# Revit family: Gleitschlitten Typ C, höhe h=200mm, Ø219 bis Ø457mm, m.D
name_source: partatom
category: HLS-Bauteile
revit_build: Autodesk Revit 2018 (Build: 20190510_1515(x64)
units: mm (PartAtom-declared; Revit-internal decimal feet)

## family parameters
Arbeitsebenenbasiert = Ja
Beim Laden mit Abzugskörper schneiden = Nein
Bemaßung runder Anschluss = Durchmesser verwenden
Gemeinsam genutzt = Ja
Immer vertikal = Nein
Klassifizierung = Keine
Raumberechnungspunkt = Nein
Teiletyp = Normal

## types (11) — shared parameters
Baustoffklasse = B2
Breite Schellenband = 50 mm
Dämmstärke = 6 mm  [stored 0.019685 ft]
Fabrikat = MEFA
Kurztext1 = Gleitschlitten C 50 x 5 mm
L = 190 mm  [stored 0.62336 ft]
Mengeneinheit = St
Schalldämmeinlage = Gummi EPDM
Sicherheitsfaktor = 1.54
Stärke Schellenband = 5 mm
Verschluss = Schraube + Mutter
Verschluss-Schraube = M12
Vorgabe-Ansicht = 1219 mm
max. Temperaturbeständigkeit = 100 °C
vpe = 1

## per-type parameters (varying)
| type | A (Breite) | Achshöhe | Artikelnummer | Breite Unterbau | EAN | Flachmaterial | Gewicht | Gewicht pro Bauteil | Kurztext2 | Länge Unterbau | RS Titan, o.D., Ø219 bis Ø457mm, 30Grad | Rohraußendurchmesser | Schuh | Stärke Material |
| Gleitschlitten TypC, h=200mm, m.D., Ø219mm | 114 mm  [stored 0.374016 ft] | 310 mm | 110cfb0219 | 253 mm | 4250928462374 | Flachmaterial nach DIN (50-5 und 70-8) : für Ø219 | 12.26 kg | 12.26 kg | 219 mm EPDM fsv | 270 mm | Rohrschelle Titan HD, Gummi,Ø219 30 Grad ok : für Ø219 | 219 mm  [stored 0.718504 ft] | TL-Fuß für Gleitschl.2Lo.14 : 9000862 | 6 mm  [stored 0.019685 ft] |
| Gleitschlitten TypC, h=200mm, m.D., Ø225mm | 114 mm  [stored 0.374016 ft] | 313 mm | 110cfb0225 | 253 mm | 4250928462381 | Flachmaterial nach DIN (50-5 und 70-8) : für Ø225 | 12.35 kg | 12.35 kg | 225 mm EPDM fsv | 270 mm | Rohrschelle Titan HD, Gummi, 30 Grad ok : für Ø225 | 225 mm  [stored 0.738189 ft] | TL-Fuß für Gleitschl.2Lo.14 : 9000862 | 6 mm  [stored 0.019685 ft] |
| Gleitschlitten TypC, h=200mm, m.D., Ø273mm | 128 mm  [stored 0.419948 ft] | 337 mm | 110cfb0273 | 269 mm | 4250928462398 | Flachmaterial nach DIN (50-5 und 70-8) : für Ø273 | 13.20 kg | 13.20 kg | 273 mm EPDM fsv | 270 mm | Rohrschelle Titan HD, Gummi, 30 Grad ok : für Ø273 | 273 mm  [stored 0.895669 ft] | TL-Fuß für Gleitschl.2Lo.14 : 9000862 | 6 mm  [stored 0.019685 ft] |
| Gleitschlitten TypC, h=200mm, m.D., Ø280mm | 128 mm  [stored 0.419948 ft] | 340 mm | 110cfb0280 | 269 mm | 4250928462404 | Flachmaterial nach DIN (50-5 und 70-8) : für Ø280 | 13.31 kg | 13.31 kg | 280 mm EPDM fsv | 270 mm | Rohrschelle Titan HD, Gummi, 30 Grad ok : für Ø280 | 280 mm  [stored 0.918635 ft] | TL-Fuß für Gleitschl.2Lo.14 : 9000862 | 6 mm  [stored 0.019685 ft] |
| Gleitschlitten TypC, h=200mm, m.D., Ø315mm | 138 mm  [stored 0.452756 ft] | 358 mm | 110cfb0315 | 280 mm | 4250928462411 | Flachmaterial nach DIN (50-5 und 70-8) : für Ø315 | 13.93 kg | 13.93 kg | 315 mm EPDM fsv | 270 mm | Rohrschelle Titan HD, Gummi, 30 Grad ok : für Ø315 | 315 mm  [stored 1.03346 ft] | TL-Fuß für Gleitschl.2Lo.14 : 9000862 | 6 mm  [stored 0.019685 ft] |
| Gleitschlitten TypC, h=200mm, m.D., Ø324mm | 138 mm  [stored 0.452756 ft] | 362 mm | 110cfb0324 | 280 mm | 4250928462428 | Flachmaterial nach DIN (50-5 und 70-8) : für Ø324 | 14.07 kg | 14.07 kg | 324 mm EPDM fsv | 270 mm | Rohrschelle Titan HD, Gummi, 30 Grad ok : für Ø324 | 324 mm  [stored 1.06299 ft] | TL-Fuß für Gleitschl.2Lo.14 : 9000862 | 6 mm  [stored 0.019685 ft] |
| Gleitschlitten TypC, h=200mm, m.D., Ø356mm | 146 mm  [stored 0.479003 ft] | 378 mm | 110cfb0356 | 290 mm | 4250928462435 | Flachmaterial nach DIN (50-5 und 70-8) : für Ø356 | 14.61 kg | 14.61 kg | 356 mm EPDM fsv | 270 mm | Rohrschelle Titan HD, Gummi, 30 Grad ok : für Ø356 | 356 mm  [stored 1.16798 ft] | TL-Fuß für Gleitschl.2Lo.14 : 9000862 | 6 mm  [stored 0.019685 ft] |
| Gleitschlitten TypC, h=200mm, m.D., Ø400mm | 177 mm  [stored 0.580709 ft] | 400 mm | 110cfb0400 | 320 mm | 4250928462442 | Flachmaterial nach DIN (50-5 und 70-8) : für Ø400 | 18.86 kg | 18.86 kg | 400 mm EPDM fsv | 270 mm | Rohrschelle Titan HD, Gummi, 30 Grad ok : für Ø400 | 400 mm  [stored 1.31234 ft] | TL-Fuß für Gleitschl.2Lo.14 : 9000863 | 8 mm  [stored 0.0262467 ft] |
| Gleitschlitten TypC, h=200mm, m.D., Ø406mm | 177 mm  [stored 0.580709 ft] | 403 mm | 110cfb0406 | 320 mm | 4250928462459 | Flachmaterial nach DIN (50-5 und 70-8) : für Ø406.4 | 18.96 kg | 18.96 kg | 406 mm EPDM fsv | 270 mm | Rohrschelle Titan HD, Gummi, 30 Grad ok : für Ø406 | 406 mm  [stored 1.33202 ft] | TL-Fuß für Gleitschl.2Lo.14 : 9000863 | 8 mm  [stored 0.0262467 ft] |
| Gleitschlitten TypC, h=200mm, m.D., Ø450mm | 189 mm  [stored 0.620079 ft] | 425 mm | 110cfb0450 | 332 mm | 4250928462466 | Flachmaterial nach DIN (50-5 und 70-8) : für Ø450 | 19.78 kg | 19.78 kg | 450 mm EPDM fsv | 270 mm | Rohrschelle Titan HD, Gummi, 30 Grad ok : für Ø450 | 450 mm  [stored 1.47638 ft] | TL-Fuß für Gleitschl.2Lo.14 : 9000863 | 8 mm  [stored 0.0262467 ft] |
| Gleitschlitten TypC, h=200mm, m.D., Ø457mm | 189 mm  [stored 0.620079 ft] | 450 mm | 110cfb0457 | 364 mm | 4250928462473 | Flachmaterial nach DIN (50-5 und 70-8) : für Ø457 | 19.90 kg | 19.90 kg | 500 mm EPDM fsv | 390 mm | Rohrschelle Titan HD, Gummi, 30 Grad ok : für Ø457 | 500 mm  [stored 1.64042 ft] | TL-Fuß für Gleitschl.2Lo.14 : 9000863 | 8 mm  [stored 0.0262467 ft] |

note: [stored X ft] marks values corroborated as IEEE doubles in the binary element streams (Revit-internal decimal feet)

## geometry (parser evidence)
native form markers: Sweep x12
no freeform markers — native parametric forms only
